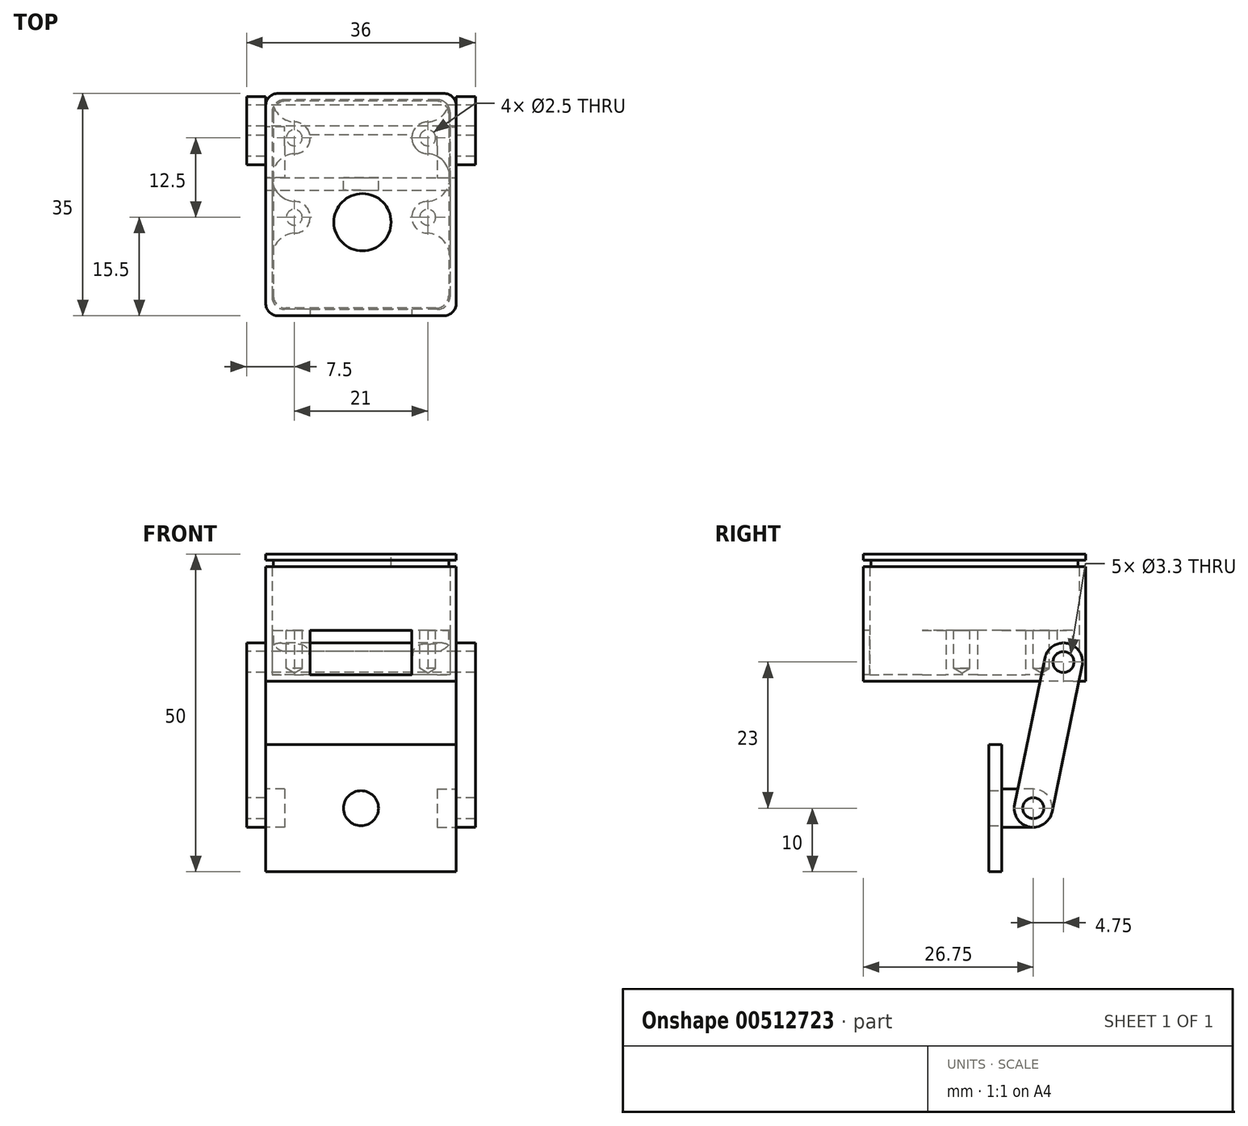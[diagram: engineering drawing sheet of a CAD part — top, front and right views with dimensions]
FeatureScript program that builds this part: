
annotation { "Feature Type Name" : "Feature", "Feature Type Description" : "" }
export const myFeature = defineFeature(function(context is Context, id is Id, definition is map)
    precondition{}
    {
        {
            var Q0;
            Q0=qCreatedBy(makeId("Top.planeOp"),FACE);
            var sketch = newSketch(context, id + "F0", { "sketchPlane" : qUnion([Q0])});
            skLineSegment(sketch, "E0.bottom", {"start": v(15, 13.25) * mm, "end": v(-15, 13.25) * mm});
            skLineSegment(sketch, "E0.top", {"start": v(15, -21.75) * mm, "end": v(-15, -21.75) * mm});
            skLineSegment(sketch, "E0.left", {"start": v(15, 13.25) * mm, "end": v(15, -21.75) * mm});
            skLineSegment(sketch, "E0.right", {"start": v(-15, 13.25) * mm, "end": v(-15, -21.75) * mm});
            skPoint(sketch, "E0.middle", {"position": v(0, -4.25) * mm});
            skPoint(sketch, "E1", {"position": v(-10.5, 6.25) * mm});
            skPoint(sketch, "E2", {"position": v(10.5, 6.25) * mm});
            skPoint(sketch, "E3", {"position": v(10.5, -6.25) * mm});
            skPoint(sketch, "E4", {"position": v(-10.5, -6.25) * mm});
            skLineSegment(sketch, "E5", {"start": v(-10.5, 6.25) * mm, "end": v(10.5, -6.25) * mm, "construction": true});
            skPoint(sketch, "E6", {"position": v(0, 0) * mm});
            skSolve(sketch);
        }
        {
            var Q0;
            Q0 = qSketchRegion(id + "F0", true);
            extrude(context, id + "F1", {"entities" : qUnion([Q0]), "depth" : 18 * mm, "offsetDistance" : 25 * mm});
        }
        {
            var Q0;
            Q0=makeQuery(id+"F1.opExtrude","CAP_FACE",FACE,{"disambiguationData":[OSD([sQuery(id+"F0.wireOp",EDGE,"E0.bottom"),sQuery(id+"F0.wireOp",EDGE,"E0.top"),sQuery(id+"F0.wireOp",EDGE,"E0.left"),sQuery(id+"F0.wireOp",EDGE,"E0.right")])],"isStart":false});
            shell(context, id + "F2", {"entities" : qUnion([Q0]), "thickness" : 1 * mm});
        }
        {
            var Q0;
            Q0=makeQuery(id+"F2.opShell","OFFSET_FACE",FACE,{"disambiguationData":[OSD([sQuery(id+"F0.wireOp",EDGE,"E0.bottom"),sQuery(id+"F0.wireOp",EDGE,"E0.top"),sQuery(id+"F0.wireOp",EDGE,"E0.left"),sQuery(id+"F0.wireOp",EDGE,"E0.right")])]});
            var sketch = newSketch(context, id + "F3", { "sketchPlane" : qUnion([Q0])});
            skCircle(sketch, "E7", {"center": v(-10.5, 6.25) * mm, "radius": 2.5 * mm});
            skCircle(sketch, "E8", {"center": v(10.5, 6.25) * mm, "radius": 2.5 * mm});
            skCircle(sketch, "E9", {"center": v(10.5, -6.25) * mm, "radius": 2.5 * mm});
            skCircle(sketch, "E10", {"center": v(-10.5, -6.25) * mm, "radius": 2.5 * mm});
            skArc(sketch, "E11", {"start": v(-14, 12.5) * mm, "mid": v(-12.99, 9.94) * mm, "end": v(-10.5, 8.75) * mm});
            skArc(sketch, "E12", {"start": v(-10.5, -8.75) * mm, "mid": v(-12.99, -9.94) * mm, "end": v(-14, -12.5) * mm});
            skArc(sketch, "E13", {"start": v(14, -12.5) * mm, "mid": v(12.99, -9.94) * mm, "end": v(10.5, -8.75) * mm});
            skArc(sketch, "E14", {"start": v(10.5, 8.75) * mm, "mid": v(12.99, 9.94) * mm, "end": v(14, 12.5) * mm});
            skLineSegment(sketch, "E15", {"start": v(-14, 12.5) * mm, "end": v(-14, -12.5) * mm});
            skLineSegment(sketch, "E16", {"start": v(14, -12.5) * mm, "end": v(14, 12.5) * mm});
            skArc(sketch, "E17", {"start": v(10.5, -3.75) * mm, "mid": v(14, 0) * mm, "end": v(10.5, 3.75) * mm});
            skArc(sketch, "E18", {"start": v(-10.5, 3.75) * mm, "mid": v(-14, 0) * mm, "end": v(-10.5, -3.75) * mm});
            skSolve(sketch);
        }
        {
            var Q0;
            Q0 = qSketchRegion(id + "F3", true);
            extrude(context, id + "F4", {"entities" : qUnion([Q0]), "operationType" : NewBodyOperationType.ADD, "depth" : 7 * mm, "offsetDistance" : 25 * mm});
        }
        {
            var Q0;
            Q0=makeQuery(id+"F1.opExtrude","SWEPT_FACE",FACE,{"disambiguationData":[OSD([sQuery(id+"F0.wireOp",EDGE,"E0.top")])]});
            var sketch = newSketch(context, id + "F5", { "sketchPlane" : qUnion([Q0])});
            skLineSegment(sketch, "E19.bottom", {"start": v(8, 8) * mm, "end": v(-8, 8) * mm});
            skLineSegment(sketch, "E19.top", {"start": v(8, 1) * mm, "end": v(-8, 1) * mm});
            skLineSegment(sketch, "E19.left", {"start": v(8, 8) * mm, "end": v(8, 1) * mm});
            skLineSegment(sketch, "E19.right", {"start": v(-8, 8) * mm, "end": v(-8, 1) * mm});
            skPoint(sketch, "E19.middle", {"position": v(0, 4.5) * mm});
            skSolve(sketch);
        }
        {
            var Q0;
            Q0 = qSketchRegion(id + "F5", true);
            extrude(context, id + "F6", {"entities" : qUnion([Q0]), "operationType" : NewBodyOperationType.REMOVE, "endBound" : BoundingType.UP_TO_NEXT, "oppositeDirection" : true, "depth" : 25 * mm, "offsetDistance" : 25 * mm});
        }
        {
            var Q0;
            Q0=makeQuery(id+"F1.opExtrude","CAP_FACE",FACE,{"disambiguationData":[OSD([sQuery(id+"F0.wireOp",EDGE,"E0.bottom"),sQuery(id+"F0.wireOp",EDGE,"E0.top"),sQuery(id+"F0.wireOp",EDGE,"E0.left"),sQuery(id+"F0.wireOp",EDGE,"E0.right")])],"isStart":false});
            var sketch = newSketch(context, id + "F7", { "sketchPlane" : qUnion([Q0])});
            skLineSegment(sketch, "E20.bottom", {"start": v(13.8, 12.05) * mm, "end": v(-13.8, 12.05) * mm});
            skLineSegment(sketch, "E20.top", {"start": v(13.8, -20.55) * mm, "end": v(-13.8, -20.55) * mm});
            skLineSegment(sketch, "E20.left", {"start": v(13.8, 12.05) * mm, "end": v(13.8, -20.55) * mm});
            skLineSegment(sketch, "E20.right", {"start": v(-13.8, 12.05) * mm, "end": v(-13.8, -20.55) * mm});
            skSolve(sketch);
        }
        {
            var Q0;
            Q0 = qSketchRegion(id + "F7", true);
            extrude(context, id + "F8", {"entities" : qUnion([Q0]), "depth" : 1 * mm, "offsetDistance" : 25 * mm});
        }
        {
            var Q0;
            Q0=makeQuery(id+"F8.opExtrude","CAP_FACE",FACE,{"disambiguationData":[OSD([sQuery(id+"F7.wireOp",EDGE,"E20.bottom"),sQuery(id+"F7.wireOp",EDGE,"E20.top"),sQuery(id+"F7.wireOp",EDGE,"E20.left"),sQuery(id+"F7.wireOp",EDGE,"E20.right")])],"isStart":false});
            var sketch = newSketch(context, id + "F9", { "sketchPlane" : qUnion([Q0])});
            skLineSegment(sketch, "E21.bottom", {"start": v(-15, -21.75) * mm, "end": v(15, -21.75) * mm});
            skLineSegment(sketch, "E21.top", {"start": v(-15, 13.25) * mm, "end": v(15, 13.25) * mm});
            skLineSegment(sketch, "E21.left", {"start": v(-15, -21.75) * mm, "end": v(-15, 13.25) * mm});
            skLineSegment(sketch, "E21.right", {"start": v(15, -21.75) * mm, "end": v(15, 13.25) * mm});
            skSolve(sketch);
        }
        {
            var Q0;
            Q0 = qSketchRegion(id + "F9", true);
            extrude(context, id + "F10", {"entities" : qUnion([Q0]), "operationType" : NewBodyOperationType.ADD, "depth" : 1 * mm, "offsetDistance" : 25 * mm});
        }
        {
            var Q0;
            Q0=makeQuery(id+"F1.opExtrude","SWEPT_FACE",FACE,{"disambiguationData":[OSD([sQuery(id+"F0.wireOp",EDGE,"E0.right")])]});
            var sketch = newSketch(context, id + "F11", { "sketchPlane" : qUnion([Q0])});
            skPoint(sketch, "E22", {"position": v(-9.75, 3) * mm});
            skCircle(sketch, "E23", {"center": v(-9.75, 3) * mm, "radius": 3 * mm});
            skLineSegment(sketch, "E24", {"start": v(-12.75, 3) * mm, "end": v(-12.75, 0) * mm});
            skLineSegment(sketch, "E25", {"start": v(-12.75, 0) * mm, "end": v(-6.75, 0) * mm});
            skLineSegment(sketch, "E26", {"start": v(-6.75, 0) * mm, "end": v(-6.75, 3) * mm});
            skSolve(sketch);
        }
        {
            var Q0;
            Q0 = qSketchRegion(id + "F11", true);
            var Q1;
            Q1=makeQuery(id+"F1.opExtrude","SWEPT_FACE",FACE,{"disambiguationData":[OSD([sQuery(id+"F0.wireOp",EDGE,"E0.left")])]});
            extrude(context, id + "F12", {"entities" : qUnion([Q0]), "operationType" : NewBodyOperationType.ADD, "endBound" : BoundingType.UP_TO_SURFACE, "oppositeDirection" : true, "depth" : 25 * mm, "endBoundEntityFace" : qUnion([Q1]), "offsetDistance" : 25 * mm});
        }
        {
            var Q0;
            Q0=makeQuery(id+"F1.opExtrude","SWEPT_EDGE",EDGE,{"disambiguationData":[OSD([sQuery(id+"F0.wireOp",EDGE,"E0.top"),sQuery(id+"F0.wireOp",EDGE,"E0.right")])]});
            var Q1;
            Q1=makeQuery(id+"F1.opExtrude","SWEPT_EDGE",EDGE,{"disambiguationData":[OSD([sQuery(id+"F0.wireOp",EDGE,"E0.top"),sQuery(id+"F0.wireOp",EDGE,"E0.left")])]});
            var Q2;
            Q2=makeQuery(id+"F1.opExtrude","SWEPT_EDGE",EDGE,{"disambiguationData":[OSD([sQuery(id+"F0.wireOp",EDGE,"E0.bottom"),sQuery(id+"F0.wireOp",EDGE,"E0.left")])]});
            var Q3;
            Q3=makeQuery(id+"F1.opExtrude","SWEPT_EDGE",EDGE,{"disambiguationData":[OSD([sQuery(id+"F0.wireOp",EDGE,"E0.bottom"),sQuery(id+"F0.wireOp",EDGE,"E0.right")])]});
            var Q4;
            Q4=makeQuery(id+"F2.opShell","OFFSET_EDGE",EDGE,{"disambiguationData":[OSD([sQuery(id+"F0.wireOp",EDGE,"E0.bottom"),sQuery(id+"F0.wireOp",EDGE,"E0.right")])]});
            var Q5;
            Q5=makeQuery(id+"F2.opShell","OFFSET_EDGE",EDGE,{"disambiguationData":[OSD([sQuery(id+"F0.wireOp",EDGE,"E0.bottom"),sQuery(id+"F0.wireOp",EDGE,"E0.left")])]});
            var Q6;
            Q6=makeQuery(id+"F2.opShell","OFFSET_EDGE",EDGE,{"disambiguationData":[OSD([sQuery(id+"F0.wireOp",EDGE,"E0.top"),sQuery(id+"F0.wireOp",EDGE,"E0.right")])]});
            var Q7;
            Q7=makeQuery(id+"F2.opShell","OFFSET_EDGE",EDGE,{"disambiguationData":[OSD([sQuery(id+"F0.wireOp",EDGE,"E0.top"),sQuery(id+"F0.wireOp",EDGE,"E0.left")])]});
            var Q8;
            Q8=makeQuery(id+"F8.opExtrude","SWEPT_EDGE",EDGE,{"disambiguationData":[OSD([sQuery(id+"F7.wireOp",EDGE,"E20.top"),sQuery(id+"F7.wireOp",EDGE,"E20.right")])]});
            var Q9;
            Q9=makeQuery(id+"F8.opExtrude","SWEPT_EDGE",EDGE,{"disambiguationData":[OSD([sQuery(id+"F7.wireOp",EDGE,"E20.top"),sQuery(id+"F7.wireOp",EDGE,"E20.left")])]});
            var Q10;
            Q10=makeQuery(id+"F8.opExtrude","SWEPT_EDGE",EDGE,{"disambiguationData":[OSD([sQuery(id+"F7.wireOp",EDGE,"E20.bottom"),sQuery(id+"F7.wireOp",EDGE,"E20.right")])]});
            var Q11;
            Q11=makeQuery(id+"F8.opExtrude","SWEPT_EDGE",EDGE,{"disambiguationData":[OSD([sQuery(id+"F7.wireOp",EDGE,"E20.bottom"),sQuery(id+"F7.wireOp",EDGE,"E20.left")])]});
            var Q12;
            Q12=makeQuery(id+"F10.opExtrude","SWEPT_EDGE",EDGE,{"disambiguationData":[OSD([sQuery(id+"F9.wireOp",EDGE,"E21.bottom"),sQuery(id+"F9.wireOp",EDGE,"E21.left")])]});
            var Q13;
            Q13=makeQuery(id+"F10.opExtrude","SWEPT_EDGE",EDGE,{"disambiguationData":[OSD([sQuery(id+"F9.wireOp",EDGE,"E21.bottom"),sQuery(id+"F9.wireOp",EDGE,"E21.right")])]});
            var Q14;
            Q14=makeQuery(id+"F10.opExtrude","SWEPT_EDGE",EDGE,{"disambiguationData":[OSD([sQuery(id+"F9.wireOp",EDGE,"E21.top"),sQuery(id+"F9.wireOp",EDGE,"E21.right")])]});
            var Q15;
            Q15=makeQuery(id+"F10.opExtrude","SWEPT_EDGE",EDGE,{"disambiguationData":[OSD([sQuery(id+"F9.wireOp",EDGE,"E21.top"),sQuery(id+"F9.wireOp",EDGE,"E21.left")])]});
            fillet(context, id + "F13", {"entities" : qUnion([Q0, Q1, Q2, Q3, Q4, Q5, Q6, Q7, Q8, Q9, Q10, Q11, Q12, Q13, Q14, Q15]), "radius" : 2 * mm, "tangentPropagation" : true, "allowEdgeOverflow" : false});
        }
        {
            var Q0;
            Q0=makeQuery(id+"F4.opExtrude","CAP_FACE",FACE,{"disambiguationData":[OSD([sQuery(id+"F3.wireOp",EDGE,"E8"),sQuery(id+"F3.wireOp",EDGE,"E14"),sQuery(id+"F3.wireOp",EDGE,"E16"),sQuery(id+"F3.wireOp",EDGE,"E17")])],"isStart":false});
            var sketch = newSketch(context, id + "F14", { "sketchPlane" : qUnion([Q0])});
            skPoint(sketch, "E27", {"position": v(-10.5, 6.25) * mm});
            skPoint(sketch, "E28", {"position": v(10.5, 6.25) * mm});
            skPoint(sketch, "E29", {"position": v(10.5, -6.25) * mm});
            skPoint(sketch, "E30", {"position": v(-10.5, -6.25) * mm});
            skSolve(sketch);
        }
        {
            var Q0;
            Q0=sQuery(id+"F14.wireOp",VERTEX,"E27");
            var Q1;
            Q1=sQuery(id+"F14.wireOp",VERTEX,"E29");
            var Q2;
            Q2=sQuery(id+"F14.wireOp",VERTEX,"E30");
            var Q3;
            Q3=sQuery(id+"F14.wireOp",VERTEX,"E28");
            var Q4;
            Q4=makeQuery(id+"F1.opExtrude","SWEPT_BODY",BODY,{"disambiguationData":[OSD([sQuery(id+"F0.wireOp",EDGE,"E0.bottom"),sQuery(id+"F0.wireOp",EDGE,"E0.top"),sQuery(id+"F0.wireOp",EDGE,"E0.left"),sQuery(id+"F0.wireOp",EDGE,"E0.right")])]});
            hole(context, id + "F15", {"style" : HoleStyle.SIMPLE, "endStyle" : HoleEndStyle.BLIND, "holeDiameter" : 2.5 * mm, "holeDepth" : 6 * mm, "isTappedThrough" : true, "tappedDepth" : 12 * mm, "tapClearance" : 3, "locations" : qUnion([Q0, Q1, Q2, Q3]), "scope" : qUnion([Q4])});
        }
        {
            var Q0;
            Q0=makeQuery(id+"F10.opExtrude","CAP_FACE",FACE,{"disambiguationData":[OSD([sQuery(id+"F9.wireOp",EDGE,"E21.bottom"),sQuery(id+"F9.wireOp",EDGE,"E21.top"),sQuery(id+"F9.wireOp",EDGE,"E21.left"),sQuery(id+"F9.wireOp",EDGE,"E21.right")])],"isStart":false});
            var sketch = newSketch(context, id + "F16", { "sketchPlane" : qUnion([Q0])});
            skLineSegment(sketch, "E31", {"start": v(-10.2, -7.02) * mm, "end": v(10.67, -7.02) * mm, "construction": true});
            skPoint(sketch, "E32", {"position": v(0.23, -7.02) * mm});
            skSolve(sketch);
        }
        {
            var Q0;
            Q0=sQuery(id+"F16.wireOp",VERTEX,"E32");
            var Q1;
            Q1=makeQuery(id+"F8.opExtrude","SWEPT_BODY",BODY,{"disambiguationData":[OSD([sQuery(id+"F7.wireOp",EDGE,"E20.bottom"),sQuery(id+"F7.wireOp",EDGE,"E20.top"),sQuery(id+"F7.wireOp",EDGE,"E20.left"),sQuery(id+"F7.wireOp",EDGE,"E20.right")])]});
            hole(context, id + "F17", {"style" : HoleStyle.SIMPLE, "endStyle" : HoleEndStyle.THROUGH, "holeDiameter" : 9 * mm, "isTappedThrough" : true, "tappedDepth" : 12 * mm, "tapClearance" : 3, "locations" : qUnion([Q0]), "scope" : qUnion([Q1])});
        }
        {
            var Q0;
            Q0=qCreatedBy(makeId("Front.planeOp"),FACE);
            var sketch = newSketch(context, id + "F18", { "sketchPlane" : qUnion([Q0])});
            skLineSegment(sketch, "E33.bottom", {"start": v(-15, -10) * mm, "end": v(15, -10) * mm});
            skLineSegment(sketch, "E33.top", {"start": v(-15, -30) * mm, "end": v(15, -30) * mm});
            skLineSegment(sketch, "E33.left", {"start": v(-15, -10) * mm, "end": v(-15, -30) * mm});
            skLineSegment(sketch, "E33.right", {"start": v(15, -10) * mm, "end": v(15, -30) * mm});
            skPoint(sketch, "E33.middle", {"position": v(0, -20) * mm});
            skSolve(sketch);
        }
        {
            var Q0;
            Q0 = qSketchRegion(id + "F18", true);
            extrude(context, id + "F19", {"entities" : qUnion([Q0]), "depth" : 2 * mm, "offsetDistance" : 25 * mm});
        }
        {
            var Q0;
            Q0=makeQuery(id+"F19.opExtrude","SWEPT_FACE",FACE,{"disambiguationData":[OSD([sQuery(id+"F18.wireOp",EDGE,"E33.left")])]});
            var sketch = newSketch(context, id + "F20", { "sketchPlane" : qUnion([Q0])});
            skPoint(sketch, "E34", {"position": v(0, -20) * mm});
            skCircle(sketch, "E35", {"center": v(-5, -20) * mm, "radius": 3 * mm});
            skLineSegment(sketch, "E36", {"start": v(-5, -23) * mm, "end": v(0, -23) * mm});
            skLineSegment(sketch, "E37", {"start": v(-5, -17) * mm, "end": v(0, -17) * mm});
            skLineSegment(sketch, "E38", {"start": v(0, -23) * mm, "end": v(0, -17) * mm});
            skSolve(sketch);
        }
        {
            var Q0;
            Q0 = qSketchRegion(id + "F20", true);
            var Q1;
            Q1=makeQuery(id+"F19.opExtrude","SWEPT_FACE",FACE,{"disambiguationData":[OSD([sQuery(id+"F18.wireOp",EDGE,"E33.right")])]});
            extrude(context, id + "F21", {"entities" : qUnion([Q0]), "oppositeDirection" : true, "depth" : 3 * mm, "endBoundEntityFace" : qUnion([Q1]), "offsetDistance" : 25 * mm});
        }
        {
            var Q0;
            {var subQ0=sQuery(id+"F20.wireOp",EDGE,"E35");var subQ1=makeQuery(id+"F20.imprint","INTERSECT",VERTEX,{"derivedFrom":[subQ0,sQuery(id+"F20.wireOp",EDGE,"E36")]});Q0=makeQuery(id+"F20.imprint","IMPRINT",FACE,{"disambiguationData":[TD([[makeQuery(id+"F20.imprint","IMPRINT",EDGE,{"disambiguationData":[TD([[subQ1,1.0]])],"derivedFrom":subQ0}),1.0]])]});}
            var sketch = newSketch(context, id + "F22", { "sketchPlane" : qUnion([Q0])});
            skCircle(sketch, "E39", {"center": v(-5, -20) * mm, "radius": 3 * mm});
            skCircle(sketch, "E40", {"center": v(-9.75, 3) * mm, "radius": 3 * mm});
            skLineSegment(sketch, "E41", {"start": v(-7.94, -20.6) * mm, "end": v(-12.69, 2.4) * mm});
            skLineSegment(sketch, "E42", {"start": v(-2.06, -19.4) * mm, "end": v(-6.81, 3.6) * mm});
            skSolve(sketch);
        }
        {
            var Q0;
            Q0 = qSketchRegion(id + "F22", true);
            extrude(context, id + "F23", {"entities" : qUnion([Q0]), "depth" : 3 * mm, "offsetDistance" : 25 * mm});
        }
        {
            var Q0;
            Q0=makeQuery(id+"F23.opExtrude","SWEPT_BODY",BODY,{"disambiguationData":[OSD([sQuery(id+"F22.wireOp",EDGE,"E39"),sQuery(id+"F22.wireOp",EDGE,"E40"),sQuery(id+"F22.wireOp",EDGE,"E41"),sQuery(id+"F22.wireOp",EDGE,"E42")])]});
            var Q1;
            Q1=makeQuery(id+"F21.opExtrude","SWEPT_BODY",BODY,{"disambiguationData":[OSD([sQuery(id+"F20.wireOp",EDGE,"E35"),sQuery(id+"F20.wireOp",EDGE,"E36"),sQuery(id+"F20.wireOp",EDGE,"E37"),sQuery(id+"F20.wireOp",EDGE,"E38")])]});
            var Q2;
            Q2=qCreatedBy(makeId("Right.planeOp"),FACE);
            mirror(context, id + "F24", {"entities" : qUnion([Q0, Q1]), "mirrorPlane" : qUnion([Q2])});
        }
        {
            var Q0;
            Q0=makeQuery(id+"F23.opExtrude","CAP_FACE",FACE,{"disambiguationData":[OSD([sQuery(id+"F22.wireOp",EDGE,"E39"),sQuery(id+"F22.wireOp",EDGE,"E40"),sQuery(id+"F22.wireOp",EDGE,"E41"),sQuery(id+"F22.wireOp",EDGE,"E42")])],"isStart":false});
            var sketch = newSketch(context, id + "F25", { "sketchPlane" : qUnion([Q0])});
            skPoint(sketch, "E43", {"position": v(-5, -20) * mm});
            skPoint(sketch, "E44", {"position": v(-9.75, 3) * mm});
            skSolve(sketch);
        }
        {
            var Q0;
            Q0=sQuery(id+"F25.wireOp",VERTEX,"E44");
            var Q1;
            Q1=sQuery(id+"F25.wireOp",VERTEX,"E43");
            var Q2;
            Q2=makeQuery(id+"F1.opExtrude","SWEPT_BODY",BODY,{"disambiguationData":[OSD([sQuery(id+"F0.wireOp",EDGE,"E0.bottom"),sQuery(id+"F0.wireOp",EDGE,"E0.top"),sQuery(id+"F0.wireOp",EDGE,"E0.left"),sQuery(id+"F0.wireOp",EDGE,"E0.right")])]});
            var Q3;
            Q3=makeQuery(id+"F23.opExtrude","SWEPT_BODY",BODY,{"disambiguationData":[OSD([sQuery(id+"F22.wireOp",EDGE,"E39"),sQuery(id+"F22.wireOp",EDGE,"E40"),sQuery(id+"F22.wireOp",EDGE,"E41"),sQuery(id+"F22.wireOp",EDGE,"E42")])]});
            var Q4;
            Q4=makeQuery(id+"F19.opExtrude","SWEPT_BODY",BODY,{"disambiguationData":[OSD([sQuery(id+"F18.wireOp",EDGE,"E33.bottom"),sQuery(id+"F18.wireOp",EDGE,"E33.top"),sQuery(id+"F18.wireOp",EDGE,"E33.left"),sQuery(id+"F18.wireOp",EDGE,"E33.right")])]});
            var Q5;
            Q5=makeQuery(id+"F24.opPattern","COPY",BODY,{"derivedFrom":makeQuery(id+"F23.opExtrude","SWEPT_BODY",BODY,{"disambiguationData":[OSD([sQuery(id+"F22.wireOp",EDGE,"E39"),sQuery(id+"F22.wireOp",EDGE,"E40"),sQuery(id+"F22.wireOp",EDGE,"E41"),sQuery(id+"F22.wireOp",EDGE,"E42")])]}),"instanceName":"1"});
            hole(context, id + "F26", {"style" : HoleStyle.SIMPLE, "endStyle" : HoleEndStyle.THROUGH, "standardTappedOrClearance" : lookupTablePath({ "standard" : "ISO", "fit" : "Normal", "size" : "M3", "type" : "Clearance" }), "standardBlindInLast" : lookupTablePath({ "fit" : "Standard", "standard" : "ISO", "size" : "M3", "type" : "Clearance" }), "holeDiameter" : 3.3 * mm, "isTappedThrough" : true, "tappedDepth" : 12 * mm, "tapClearance" : 3, "locations" : qUnion([Q0, Q1]), "scope" : qUnion([Q2, Q3, Q4, Q5])});
        }
        {
            var Q0;
            Q0=sQuery(id+"F18.wireOp",VERTEX,"E33.middle");
            var Q1;
            Q1=makeQuery(id+"F19.opExtrude","SWEPT_BODY",BODY,{"disambiguationData":[OSD([sQuery(id+"F18.wireOp",EDGE,"E33.bottom"),sQuery(id+"F18.wireOp",EDGE,"E33.top"),sQuery(id+"F18.wireOp",EDGE,"E33.left"),sQuery(id+"F18.wireOp",EDGE,"E33.right")])]});
            hole(context, id + "F27", {"style" : HoleStyle.SIMPLE, "endStyle" : HoleEndStyle.THROUGH, "oppositeDirection" : true, "standardTappedOrClearance" : lookupTablePath({ "standard" : "ISO", "fit" : "Normal", "size" : "M5", "type" : "Clearance" }), "standardBlindInLast" : lookupTablePath({ "fit" : "Standard", "standard" : "ISO", "size" : "M5", "type" : "Clearance" }), "holeDiameter" : 5.5 * mm, "isTappedThrough" : true, "tappedDepth" : 12 * mm, "tapClearance" : 3, "locations" : qUnion([Q0]), "scope" : qUnion([Q1])});
        }
    });
